# Revit family: ShowerHead-SlidingHandshowerSet-Master-1F-Vitra-AquaHeatSeries-A45693
name_source: partatom
category: Plumbing Fixtures
revit_build: Autodesk Revit 2017 (Build: 20160225_1515(x64)
units: mm (PartAtom-declared; Revit-internal decimal feet)

## family parameters
Always vertical = No
Cut with Voids When Loaded = No
OmniClass Number = 23.45.55.17
OmniClass Title = Mixing Faucets
Part Type = Normal
Room Calculation Point = No
Round Connector Dimension = Use Diameter
Shared = Yes
Work Plane-Based = No

## types (6) — shared parameters
BIMobject category = Bath/Shower Mixer
CW Connection = No
Coating Material = Chrome
Color = Chrome
Connection Diameter (mm) = 15 mm  [stored 0.0492126 ft]
Depth(mm) = 180 mm  [stored 0.590551 ft]
Description = Sliding Hand Shower Set - 1F
Design country = Turkey
HW Connection = No
Height(mm) = 700 mm  [stored 2.29659 ft]
IFC Classification = Sanitary Terminal
Manufacturer = Vitra
Manufacturer name = Vitra
Masterformat 2014 Code = 22 41 23
Masterformat 2014 Description = Residential Showers
MountingType = Wall-mounted
NBS Referans Code = 35-06-81
NBS Referans Description = Shower Heads
Nominal height = 0.000
Nominal width = 0.000
Number Of Connections = 1 mm  [stored 0.00328084 ft]
OmniClass Code = 23-31 17 19
OmniClass Description = Shower Head Fixtures
Product Properties = Sliding Hand Shower Set
Product Type = Sliding Hand Shower Set
Product certification = https://vitraglobal.com
Product family = Shower System
Product group = HandshowerSet
Range of flow pressure = 0.5-10 bar (Recommended 3-5 Bars)
Secondary Material = Plastic
Third Material = Plastic1
UNSPSC Code = 30181503
URL = https://vitraglobal.com
Uniclass 1.4 Code = L7214
Uniclass 1.4 Description = Showers
Uniclass 2.0 Code = PR-35-06-81
Uniclass 2.0 Description = Shower Heads
Uniclass 2015 Code = Pr_40_20_87_76
Uniclass 2015 Name = Shower heads
Uniformat II Code = D2010
Uniformat II Description = Plumbing Fixtures
Vent Connection = No
Warranty Period (Year) = 5 Years
Waste Connection = No
Weight Net (kg) = 1,431
Width(mm) = 280 mm  [stored 0.918635 ft]
Youtube = https://www.youtube.com
zero-valued in all types: CWFU, Cost, HWFU, WFU

## per-type parameters (varying)
| type | Article No. (default) | Brand | Model | Product Manual | Product SKU | Product data url | Technical description |
| ShowerHead-SlidingHandshowerSet-Master-1F-Vitra-AquaHeatSeries-A45693 | A45693 | Artema | A45693 |  | A45693 | https://www.vitra.com.tr | https://www.vitra.com.tr |
| ShowerHead-SlidingHandshowerSet-Master-1F-Vitra-AquaHeatSeries-A45693EKM | A45693EKM | VitrA | A45693EKM |  | A45693EKM | https://www.vitra-bad.fr | http://cdn.vitra.com.tr |
| ShowerHead-SlidingHandshowerSet-Master-1F-Vitra-AquaHeatSeries-A45693EXP | A45693EXP | VitrA | A45693EXP |  | A45693EXP | https://www.vitra-bad.fr | http://cdn.vitra.com.tr |
| ShowerHead-SlidingHandshowerSet-Master-1F-Vitra-AquaHeatSeries-A45693EXPS | A45693EXPS | VitrA | A45693EXPS |  | A45693EXPS | https://www.vitra-bad.fr | http://cdn.vitra.com.tr |
| ShowerHead-SlidingHandshowerSet-Master-1F-Vitra-AquaHeatSeries-A45693IND | A45693IND | VitrA | A45693IND | Water Saving, Easy Cleaning, Easy Installation | A45693IND | https://www.vitra-india.com |  |
| ShowerHead-SlidingHandshowerSet-Master-1F-Vitra-AquaHeatSeries-A45693TPX | A45693TPX | VitrA | A45693TPX |  | A45693TPX | https://www.vitra-bad.fr | http://cdn.vitra.com.tr |

note: [stored X ft] marks values corroborated as IEEE doubles in the binary element streams (Revit-internal decimal feet)

## geometry (parser evidence)
native form markers: Sweep x3
no freeform markers — native parametric forms only
